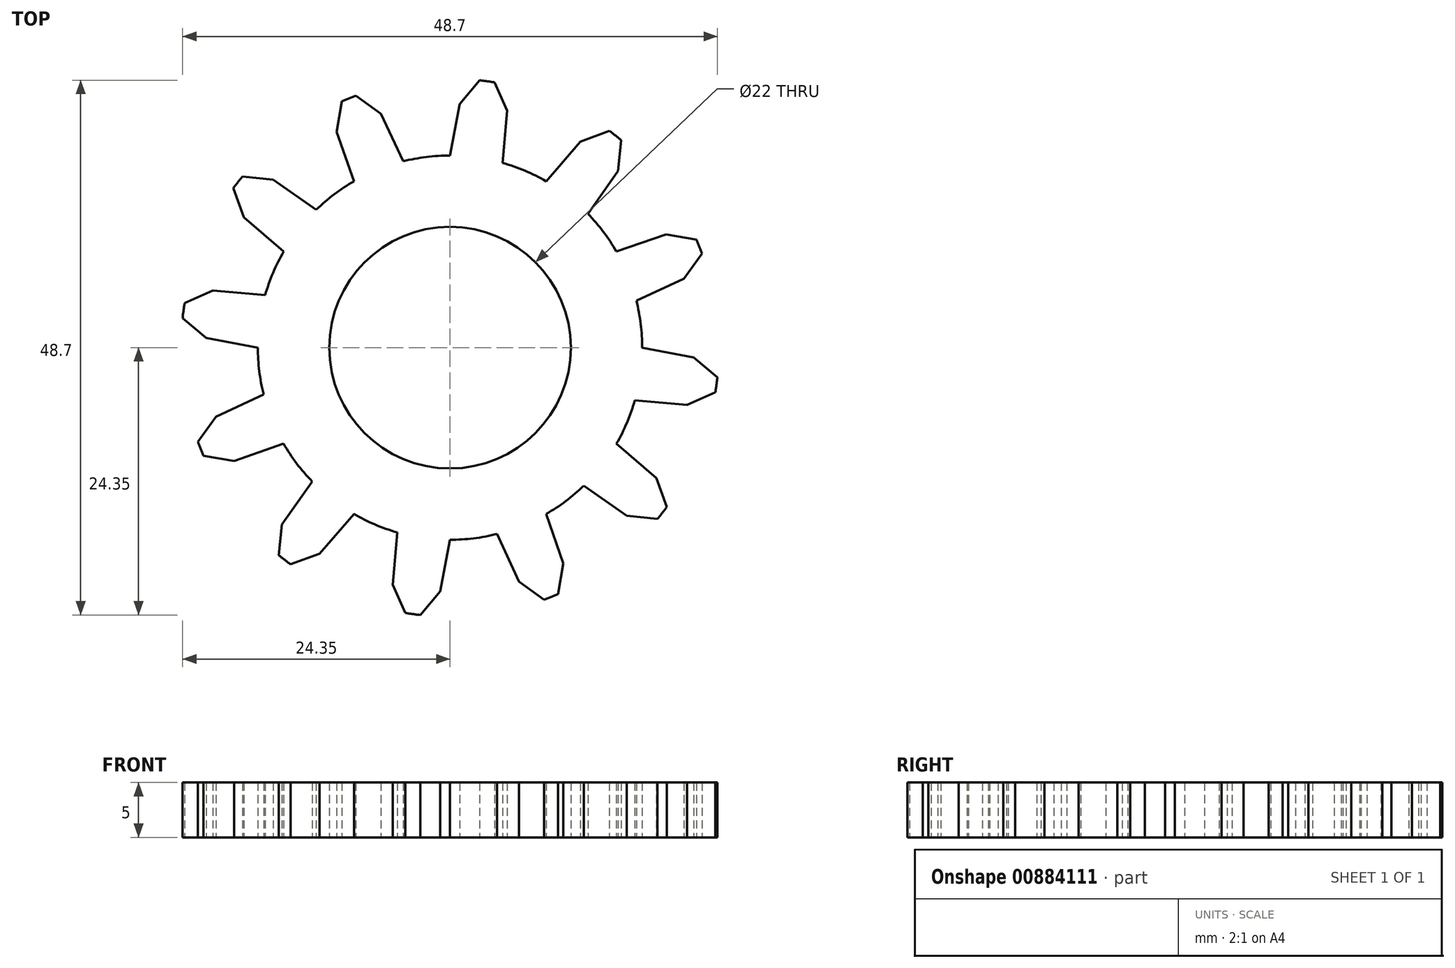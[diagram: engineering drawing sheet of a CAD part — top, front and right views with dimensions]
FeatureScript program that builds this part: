
annotation { "Feature Type Name" : "Feature", "Feature Type Description" : "" }
export const myFeature = defineFeature(function(context is Context, id is Id, definition is map)
    precondition{}
    {
        {
            var Q0;
            Q0=qCreatedBy(makeId("Top.planeOp"),FACE);
            var sketch = newSketch(context, id + "F0", { "sketchPlane" : qUnion([Q0])});
            skCircle(sketch, "E0", {"center": v(0, 0) * mm, "radius": 11 * mm});
            skCircle(sketch, "E1", {"center": v(0, 0) * mm, "radius": 17.5 * mm});
            skArc(sketch, "E2", {"start": v(4.06, 24.16) * mm, "mid": v(3.38, 24.27) * mm, "end": v(2.7, 24.35) * mm});
            skLineSegment(sketch, "E3", {"start": v(0, 17.5) * mm, "end": v(0.9, 22.2) * mm});
            skLineSegment(sketch, "E4", {"start": v(0.9, 22.2) * mm, "end": v(2.7, 24.35) * mm});
            skLineSegment(sketch, "E5", {"start": v(0, 0) * mm, "end": v(3.38, 24.27) * mm, "construction": true});
            skLineSegment(sketch, "E6.MirrorCS", {"start": v(4.79, 16.83) * mm, "end": v(5.21, 21.6) * mm});
            skLineSegment(sketch, "E7.MirrorCS", {"start": v(5.21, 21.6) * mm, "end": v(4.06, 24.16) * mm});
            skLineSegment(sketch, "E8.1.0", {"start": v(-4.27, 16.97) * mm, "end": v(-6.28, 21.3) * mm});
            skLineSegment(sketch, "E8.1.1", {"start": v(-6.28, 21.3) * mm, "end": v(-8.57, 22.95) * mm});
            skArc(sketch, "E8.1.2", {"start": v(-8.57, 22.95) * mm, "mid": v(-9.2, 22.7) * mm, "end": v(-9.83, 22.44) * mm});
            skLineSegment(sketch, "E8.1.3", {"start": v(-10.33, 19.67) * mm, "end": v(-9.83, 22.44) * mm});
            skLineSegment(sketch, "E8.1.4", {"start": v(-8.75, 15.16) * mm, "end": v(-10.33, 19.67) * mm});
            skLineSegment(sketch, "E8.2.0", {"start": v(-12.18, 12.56) * mm, "end": v(-16.1, 15.31) * mm});
            skLineSegment(sketch, "E8.2.1", {"start": v(-16.1, 15.31) * mm, "end": v(-18.9, 15.6) * mm});
            skArc(sketch, "E8.2.2", {"start": v(-18.9, 15.6) * mm, "mid": v(-19.32, 15.06) * mm, "end": v(-19.74, 14.52) * mm});
            skLineSegment(sketch, "E8.2.3", {"start": v(-18.77, 11.87) * mm, "end": v(-19.74, 14.52) * mm});
            skLineSegment(sketch, "E8.2.4", {"start": v(-15.16, 8.75) * mm, "end": v(-18.77, 11.87) * mm});
            skLineSegment(sketch, "E8.3.0", {"start": v(-16.83, 4.79) * mm, "end": v(-21.6, 5.21) * mm});
            skLineSegment(sketch, "E8.3.1", {"start": v(-21.6, 5.21) * mm, "end": v(-24.16, 4.06) * mm});
            skArc(sketch, "E8.3.2", {"start": v(-24.16, 4.06) * mm, "mid": v(-24.27, 3.38) * mm, "end": v(-24.35, 2.7) * mm});
            skLineSegment(sketch, "E8.3.3", {"start": v(-22.2, 0.9) * mm, "end": v(-24.35, 2.7) * mm});
            skLineSegment(sketch, "E8.3.4", {"start": v(-17.5, 0) * mm, "end": v(-22.2, 0.9) * mm});
            skLineSegment(sketch, "E8.4.0", {"start": v(-16.97, -4.27) * mm, "end": v(-21.3, -6.28) * mm});
            skLineSegment(sketch, "E8.4.1", {"start": v(-21.3, -6.28) * mm, "end": v(-22.95, -8.57) * mm});
            skArc(sketch, "E8.4.2", {"start": v(-22.95, -8.57) * mm, "mid": v(-22.7, -9.2) * mm, "end": v(-22.44, -9.83) * mm});
            skLineSegment(sketch, "E8.4.3", {"start": v(-19.67, -10.33) * mm, "end": v(-22.44, -9.83) * mm});
            skLineSegment(sketch, "E8.4.4", {"start": v(-15.16, -8.75) * mm, "end": v(-19.67, -10.33) * mm});
            skLineSegment(sketch, "E8.5.0", {"start": v(-12.56, -12.18) * mm, "end": v(-15.31, -16.1) * mm});
            skLineSegment(sketch, "E8.5.1", {"start": v(-15.31, -16.1) * mm, "end": v(-15.6, -18.9) * mm});
            skArc(sketch, "E8.5.2", {"start": v(-15.6, -18.9) * mm, "mid": v(-15.06, -19.32) * mm, "end": v(-14.52, -19.74) * mm});
            skLineSegment(sketch, "E8.5.3", {"start": v(-11.87, -18.77) * mm, "end": v(-14.52, -19.74) * mm});
            skLineSegment(sketch, "E8.5.4", {"start": v(-8.75, -15.16) * mm, "end": v(-11.87, -18.77) * mm});
            skLineSegment(sketch, "E8.6.0", {"start": v(-4.79, -16.83) * mm, "end": v(-5.21, -21.6) * mm});
            skLineSegment(sketch, "E8.6.1", {"start": v(-5.21, -21.6) * mm, "end": v(-4.06, -24.16) * mm});
            skArc(sketch, "E8.6.2", {"start": v(-4.06, -24.16) * mm, "mid": v(-3.38, -24.27) * mm, "end": v(-2.7, -24.35) * mm});
            skLineSegment(sketch, "E8.6.3", {"start": v(-0.9, -22.2) * mm, "end": v(-2.7, -24.35) * mm});
            skLineSegment(sketch, "E8.6.4", {"start": v(0, -17.5) * mm, "end": v(-0.9, -22.2) * mm});
            skLineSegment(sketch, "E8.7.0", {"start": v(4.27, -16.97) * mm, "end": v(6.28, -21.3) * mm});
            skLineSegment(sketch, "E8.7.1", {"start": v(6.28, -21.3) * mm, "end": v(8.57, -22.95) * mm});
            skArc(sketch, "E8.7.2", {"start": v(8.57, -22.95) * mm, "mid": v(9.2, -22.7) * mm, "end": v(9.83, -22.44) * mm});
            skLineSegment(sketch, "E8.7.3", {"start": v(10.33, -19.67) * mm, "end": v(9.83, -22.44) * mm});
            skLineSegment(sketch, "E8.7.4", {"start": v(8.75, -15.16) * mm, "end": v(10.33, -19.67) * mm});
            skLineSegment(sketch, "E8.8.0", {"start": v(12.18, -12.56) * mm, "end": v(16.1, -15.31) * mm});
            skLineSegment(sketch, "E8.8.1", {"start": v(16.1, -15.31) * mm, "end": v(18.9, -15.6) * mm});
            skArc(sketch, "E8.8.2", {"start": v(18.9, -15.6) * mm, "mid": v(19.32, -15.06) * mm, "end": v(19.74, -14.52) * mm});
            skLineSegment(sketch, "E8.8.3", {"start": v(18.77, -11.87) * mm, "end": v(19.74, -14.52) * mm});
            skLineSegment(sketch, "E8.8.4", {"start": v(15.16, -8.75) * mm, "end": v(18.77, -11.87) * mm});
            skLineSegment(sketch, "E8.9.0", {"start": v(16.83, -4.79) * mm, "end": v(21.6, -5.21) * mm});
            skLineSegment(sketch, "E8.9.1", {"start": v(21.6, -5.21) * mm, "end": v(24.16, -4.06) * mm});
            skArc(sketch, "E8.9.2", {"start": v(24.16, -4.06) * mm, "mid": v(24.27, -3.38) * mm, "end": v(24.35, -2.7) * mm});
            skLineSegment(sketch, "E8.9.3", {"start": v(22.2, -0.9) * mm, "end": v(24.35, -2.7) * mm});
            skLineSegment(sketch, "E8.9.4", {"start": v(17.5, 0) * mm, "end": v(22.2, -0.9) * mm});
            skLineSegment(sketch, "E8.10.0", {"start": v(16.97, 4.27) * mm, "end": v(21.3, 6.28) * mm});
            skLineSegment(sketch, "E8.10.1", {"start": v(21.3, 6.28) * mm, "end": v(22.95, 8.57) * mm});
            skArc(sketch, "E8.10.2", {"start": v(22.95, 8.57) * mm, "mid": v(22.7, 9.2) * mm, "end": v(22.44, 9.83) * mm});
            skLineSegment(sketch, "E8.10.3", {"start": v(19.67, 10.33) * mm, "end": v(22.44, 9.83) * mm});
            skLineSegment(sketch, "E8.10.4", {"start": v(15.16, 8.75) * mm, "end": v(19.67, 10.33) * mm});
            skLineSegment(sketch, "E8.11.0", {"start": v(12.56, 12.18) * mm, "end": v(15.31, 16.1) * mm});
            skLineSegment(sketch, "E8.11.1", {"start": v(15.31, 16.1) * mm, "end": v(15.6, 18.9) * mm});
            skArc(sketch, "E8.11.2", {"start": v(15.6, 18.9) * mm, "mid": v(15.06, 19.32) * mm, "end": v(14.52, 19.74) * mm});
            skLineSegment(sketch, "E8.11.3", {"start": v(11.87, 18.77) * mm, "end": v(14.52, 19.74) * mm});
            skLineSegment(sketch, "E8.11.4", {"start": v(8.75, 15.16) * mm, "end": v(11.87, 18.77) * mm});
            skSolve(sketch);
        }
        {
            var Q0;
            Q0 = qSketchRegion(id + "F0", true);
            extrude(context, id + "F1", {"entities" : qUnion([Q0]), "depth" : 5 * mm, "offsetDistance" : 25 * mm});
        }
    });
